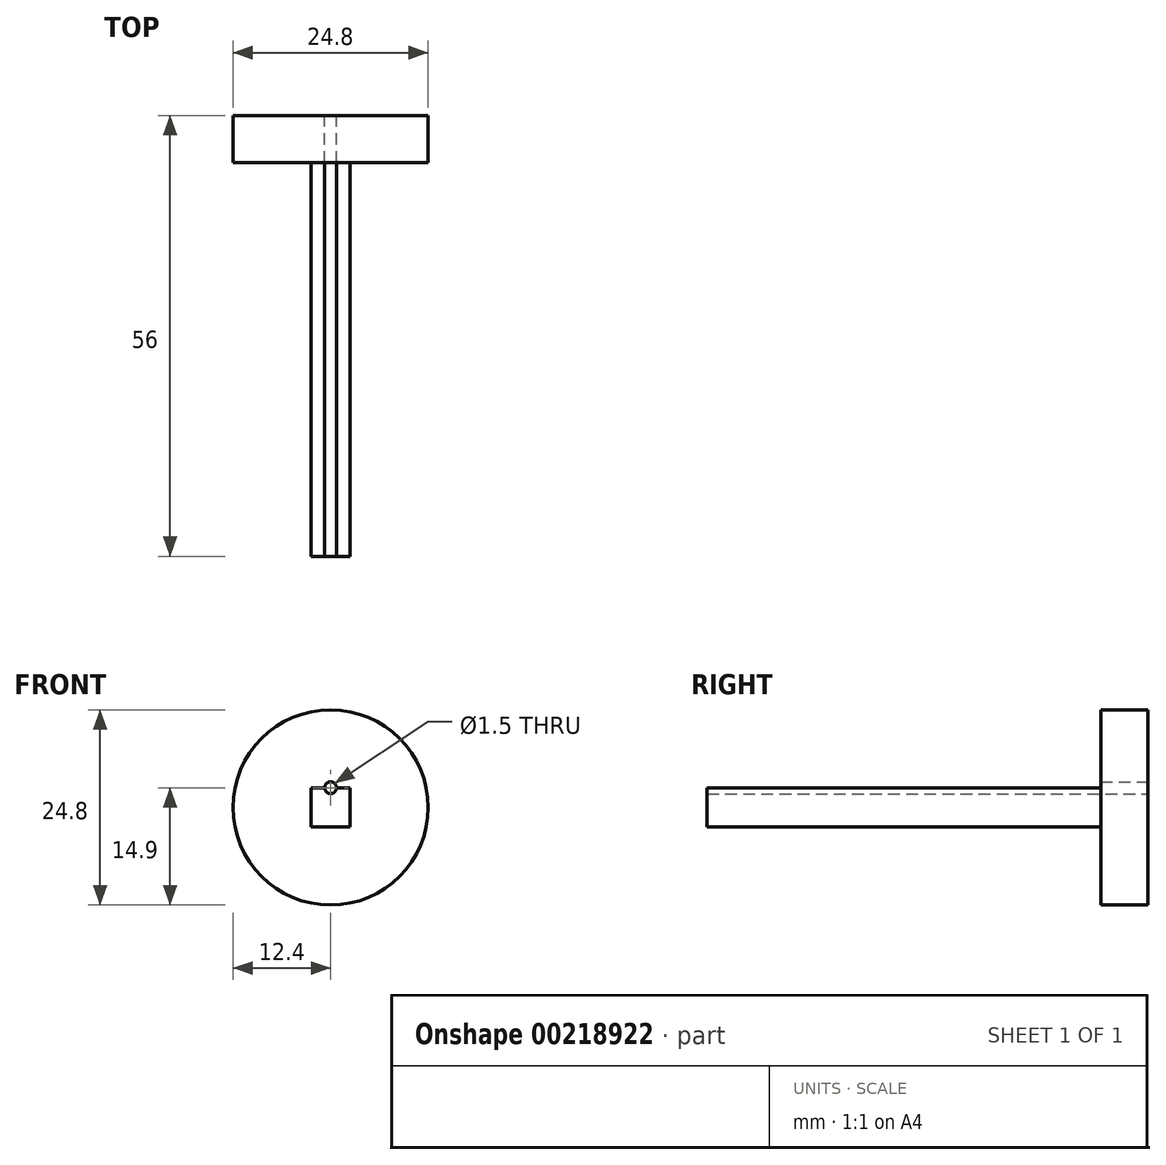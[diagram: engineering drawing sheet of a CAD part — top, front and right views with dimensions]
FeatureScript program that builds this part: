
annotation { "Feature Type Name" : "Feature", "Feature Type Description" : "" }
export const myFeature = defineFeature(function(context is Context, id is Id, definition is map)
    precondition{}
    {
        {
            var Q0;
            Q0=qCreatedBy(makeId("Front.planeOp"),FACE);
            var sketch = newSketch(context, id + "F0", { "sketchPlane" : qUnion([Q0])});
            skCircle(sketch, "E0", {"center": v(0, 0) * mm, "radius": 12.4 * mm});
            skSolve(sketch);
        }
        {
            var Q0;
            Q0 = qSketchRegion(id + "F0", true);
            extrude(context, id + "F1", {"entities" : qUnion([Q0]), "depth" : 6 * mm});
        }
        {
            var Q0;
            Q0=makeQuery(id+"F1.opExtrude","CAP_FACE",FACE,{"disambiguationData":[OSD([sQuery(id+"F0.wireOp",EDGE,"E0")])],"isStart":false});
            var sketch = newSketch(context, id + "F2", { "sketchPlane" : qUnion([Q0])});
            skLineSegment(sketch, "E1.bottom", {"start": v(2.5, -2.5) * mm, "end": v(-2.5, -2.5) * mm});
            skLineSegment(sketch, "E1.top", {"start": v(2.5, 2.5) * mm, "end": v(-2.5, 2.5) * mm});
            skLineSegment(sketch, "E1.left", {"start": v(2.5, -2.5) * mm, "end": v(2.5, 2.5) * mm});
            skLineSegment(sketch, "E1.right", {"start": v(-2.5, -2.5) * mm, "end": v(-2.5, 2.5) * mm});
            skPoint(sketch, "E1.middle", {"position": v(0, 0) * mm});
            skSolve(sketch);
        }
        {
            var Q0;
            Q0=makeQuery(id+"F2.imprint","IMPRINT",FACE,{"disambiguationData":[TD([[makeQuery(id+"F2.imprint","IMPRINT",EDGE,{"derivedFrom":sQuery(id+"F2.wireOp",EDGE,"E1.bottom")}),-1.0]])]});
            extrude(context, id + "F3", {"entities" : qUnion([Q0]), "operationType" : NewBodyOperationType.ADD, "depth" : 50 * mm});
        }
        {
            var Q0;
            Q0=makeQuery(id+"F1.opExtrude","CAP_FACE",FACE,{"disambiguationData":[OSD([sQuery(id+"F0.wireOp",EDGE,"E0")])],"isStart":true});
            var sketch = newSketch(context, id + "F4", { "sketchPlane" : qUnion([Q0])});
            skCircle(sketch, "E2", {"center": v(0, 2.5) * mm, "radius": 0.75 * mm});
            skSolve(sketch);
        }
        {
            var Q0;
            Q0 = qSketchRegion(id + "F4", true);
            extrude(context, id + "F5", {"entities" : qUnion([Q0]), "operationType" : NewBodyOperationType.REMOVE, "oppositeDirection" : true, "depth" : 60 * mm});
        }
    });
